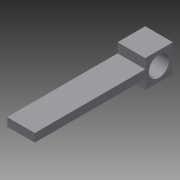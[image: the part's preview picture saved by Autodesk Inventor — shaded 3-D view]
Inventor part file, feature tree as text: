
AUTODESK INVENTOR PART (.ipt)
format: ipt  version: 2015 (Build 190159000, 159)  size: 95,232 bytes
history: native  units: in
note: dims shown in document units (in); Inventor stores cm internally (conversion verified against a paired STEP export)
features: extrude x3, sketch x3
ambient origin geometry x8: Origin, YZ Plane, XZ Plane, XY Plane, X Axis, Y Axis, Z Axis, Center Point
bodies: Solid1 (feature_tree)
feature tree (6):
  extrude  "Extrusion1"  Depth=0.25in
  extrude  "Extrusion2"  Depth=0.25in
  extrude  "Extrusion3"  Depth=0.1625in
  sketch  "Sketch1"  dims[d0=0.075in d1=0.25in]
  sketch  "Sketch2"  dims[d2=1.25in d3=0.0in d4=0.25in]
  sketch  "Sketch3"  dims[d5=0.0875in d6=0.1625in d7=0.0in d8=0.0in d9=0.125in d11=0.125in d12=0.1838in d13=0.125in d14=0.0in]
